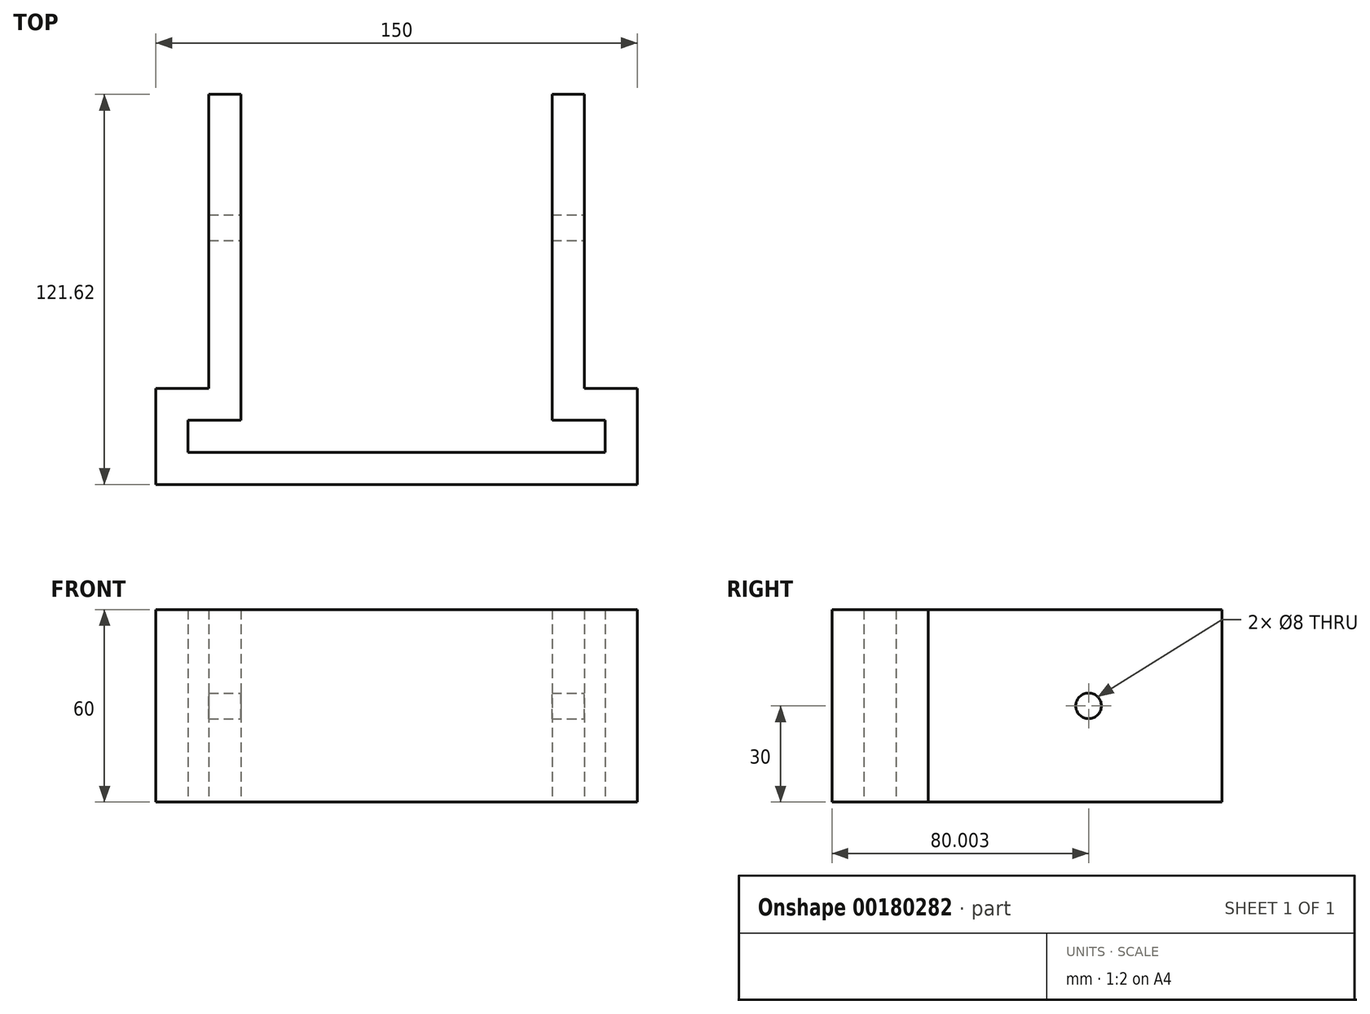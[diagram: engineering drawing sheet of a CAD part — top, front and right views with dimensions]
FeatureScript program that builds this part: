
annotation { "Feature Type Name" : "Feature", "Feature Type Description" : "" }
export const myFeature = defineFeature(function(context is Context, id is Id, definition is map)
    precondition{}
    {
        {
            var Q0;
            Q0=qCreatedBy(makeId("Top.planeOp"),FACE);
            var sketch = newSketch(context, id + "F0", { "sketchPlane" : qUnion([Q0])});
            skLineSegment(sketch, "E0", {"start": v(-44.2, -65.6) * mm, "end": v(105.8, -65.6) * mm});
            skLineSegment(sketch, "E1", {"start": v(105.8, -65.6) * mm, "end": v(105.8, -35.6) * mm});
            skLineSegment(sketch, "E2", {"start": v(105.8, -35.6) * mm, "end": v(89.3, -35.6) * mm});
            skLineSegment(sketch, "E3", {"start": v(89.3, -35.6) * mm, "end": v(89.3, 56.01) * mm});
            skLineSegment(sketch, "E4", {"start": v(89.3, 56.01) * mm, "end": v(79.3, 56.01) * mm});
            skLineSegment(sketch, "E5", {"start": v(79.3, 56.01) * mm, "end": v(79.3, -45.6) * mm});
            skLineSegment(sketch, "E6", {"start": v(79.3, -45.6) * mm, "end": v(95.8, -45.6) * mm});
            skLineSegment(sketch, "E7", {"start": v(95.8, -45.6) * mm, "end": v(95.8, -55.6) * mm});
            skLineSegment(sketch, "E8", {"start": v(95.8, -55.6) * mm, "end": v(-34.2, -55.6) * mm});
            skLineSegment(sketch, "E9", {"start": v(-34.2, -55.6) * mm, "end": v(-34.2, -45.6) * mm});
            skLineSegment(sketch, "E10", {"start": v(-34.2, -45.6) * mm, "end": v(-17.7, -45.6) * mm});
            skLineSegment(sketch, "E11", {"start": v(-17.7, -45.6) * mm, "end": v(-17.7, 56.01) * mm});
            skLineSegment(sketch, "E12", {"start": v(-17.7, 56.01) * mm, "end": v(-27.7, 56.01) * mm});
            skLineSegment(sketch, "E13", {"start": v(-27.7, 56.01) * mm, "end": v(-27.7, -35.6) * mm});
            skLineSegment(sketch, "E14", {"start": v(-27.7, -35.6) * mm, "end": v(-44.2, -35.6) * mm});
            skLineSegment(sketch, "E15", {"start": v(-44.2, -35.6) * mm, "end": v(-44.2, -65.6) * mm});
            skSolve(sketch);
        }
        {
            var Q0;
            Q0=makeQuery(id+"F0.imprint","IMPRINT",FACE,{"disambiguationData":[TD([[makeQuery(id+"F0.imprint","IMPRINT",EDGE,{"derivedFrom":sQuery(id+"F0.wireOp",EDGE,"E0")}),1.0]])]});
            extrude(context, id + "F1", {"entities" : qUnion([Q0]), "depth" : 60 * mm});
        }
        {
            var Q0;
            Q0=makeQuery(id+"F1.opExtrude","SWEPT_FACE",FACE,{"disambiguationData":[OSD([sQuery(id+"F0.wireOp",EDGE,"E3")])]});
            var sketch = newSketch(context, id + "F2", { "sketchPlane" : qUnion([Q0])});
            skCircle(sketch, "E16", {"center": v(14.4, 30) * mm, "radius": 4 * mm});
            skSolve(sketch);
        }
        {
            var Q0;
            Q0=makeQuery(id+"F2.imprint","IMPRINT",FACE,{"disambiguationData":[TD([[makeQuery(id+"F2.imprint","IMPRINT",EDGE,{"derivedFrom":sQuery(id+"F2.wireOp",EDGE,"E16")}),1.0]])]});
            extrude(context, id + "F3", {"entities" : qUnion([Q0]), "operationType" : NewBodyOperationType.REMOVE, "oppositeDirection" : true, "depth" : 154 * mm});
        }
    });
